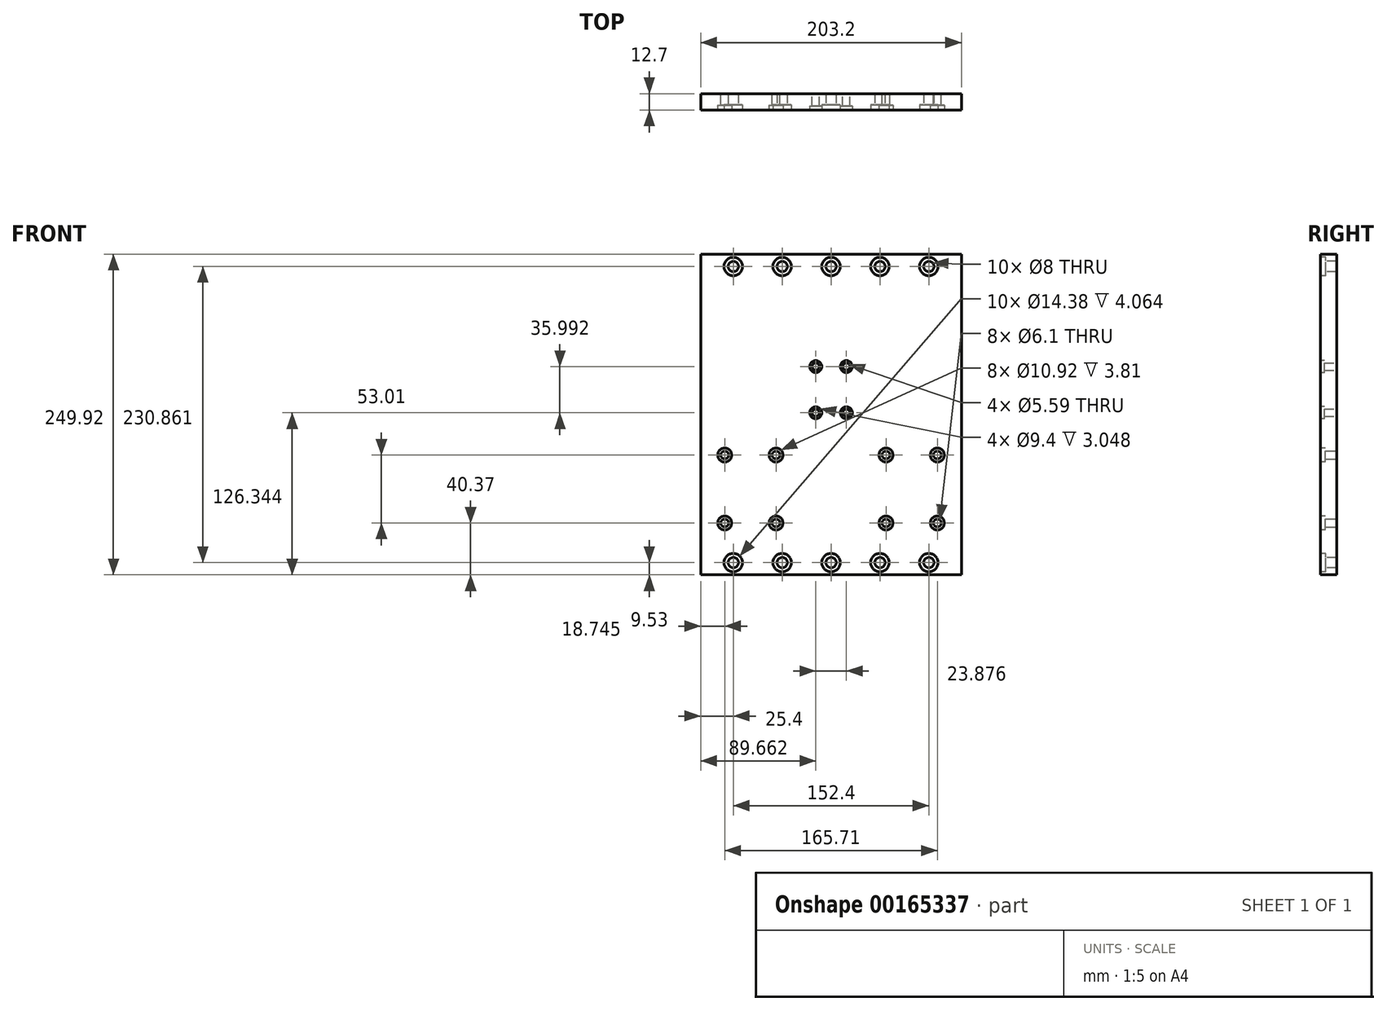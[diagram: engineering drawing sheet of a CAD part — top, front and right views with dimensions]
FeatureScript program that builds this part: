
annotation { "Feature Type Name" : "Feature", "Feature Type Description" : "" }
export const myFeature = defineFeature(function(context is Context, id is Id, definition is map)
    precondition{}
    {
        {
            var Q0;
            Q0=qCreatedBy(makeId("Front.planeOp"),FACE);
            var sketch = newSketch(context, id + "F0", { "sketchPlane" : qUnion([Q0])});
            skLineSegment(sketch, "E0.rect.bottom", {"start": v(101.6, 124.96) * mm, "end": v(-101.6, 124.96) * mm});
            skLineSegment(sketch, "E0.rect.top", {"start": v(101.6, -124.96) * mm, "end": v(-101.6, -124.96) * mm});
            skLineSegment(sketch, "E0.rect.left", {"start": v(101.6, 124.96) * mm, "end": v(101.6, -124.96) * mm});
            skLineSegment(sketch, "E0.rect.right", {"start": v(-101.6, 124.96) * mm, "end": v(-101.6, -124.96) * mm});
            skPoint(sketch, "E0.rect.middle", {"position": v(0, 0) * mm});
            skLineSegment(sketch, "E1", {"start": v(101.6, 112.26) * mm, "end": v(-101.6, 112.26) * mm, "construction": true});
            skLineSegment(sketch, "E2", {"start": v(101.6, -112.26) * mm, "end": v(-101.6, -112.26) * mm, "construction": true});
            skLineSegment(sketch, "E3", {"start": v(-11.94, 124.96) * mm, "end": v(-11.94, -124.96) * mm, "construction": true});
            skLineSegment(sketch, "E4.bottom", {"start": v(-11.94, 112.26) * mm, "end": v(11.94, 112.26) * mm, "construction": true});
            skLineSegment(sketch, "E4.left", {"start": v(-11.94, 112.26) * mm, "end": v(-11.94, 76.26) * mm, "construction": true});
            skLineSegment(sketch, "E4.right", {"start": v(11.94, 112.26) * mm, "end": v(11.94, 76.26) * mm, "construction": true});
            skLineSegment(sketch, "E5", {"start": v(11.94, 124.96) * mm, "end": v(11.94, -124.96) * mm, "construction": true});
            skLineSegment(sketch, "E6", {"start": v(-101.6, 1.38) * mm, "end": v(101.6, 1.38) * mm, "construction": true});
            skLineSegment(sketch, "E7", {"start": v(-101.6, 37.38) * mm, "end": v(101.6, 37.38) * mm, "construction": true});
            skCircle(sketch, "E8", {"center": v(-11.94, 37.38) * mm, "radius": 2.8 * mm});
            skCircle(sketch, "E9", {"center": v(11.94, 37.38) * mm, "radius": 2.8 * mm});
            skCircle(sketch, "E10", {"center": v(-11.94, 1.38) * mm, "radius": 2.8 * mm});
            skCircle(sketch, "E11", {"center": v(11.94, 1.38) * mm, "radius": 2.8 * mm});
            skSolve(sketch);
        }
        {
            var Q0;
            Q0=qSketchRegion(id+"F0",true);
            extrude(context, id + "F1", {"entities" : qUnion([Q0]), "depth" : 12.7 * mm});
        }
        {
            var Q0;
            Q0=makeQuery(id+"F1.opExtrude","CAP_FACE",FACE,{"disambiguationData":[OSD([sQuery(id+"F0.wireOp",EDGE,"E0.rect.bottom"),sQuery(id+"F0.wireOp",EDGE,"E0.rect.top"),sQuery(id+"F0.wireOp",EDGE,"E0.rect.left"),sQuery(id+"F0.wireOp",EDGE,"E0.rect.right"),sQuery(id+"F0.wireOp",EDGE,"8fd6003c-c3e5-4104-bfaa-be9952ec9e42"),sQuery(id+"F0.wireOp",EDGE,"85de903b-7077-4fb2-a5dd-9b00dc729731"),sQuery(id+"F0.wireOp",EDGE,"d51e1711-b5ba-43c6-b441-8d78bd74f6b7"),sQuery(id+"F0.wireOp",EDGE,"2b9548f0-683a-4c88-97d9-80483cf9402c")])],"isStart":false});
            var sketch = newSketch(context, id + "F2", { "sketchPlane" : qUnion([Q0])});
            skLineSegment(sketch, "E12", {"start": v(-101.6, 115.43) * mm, "end": v(101.6, 115.43) * mm, "construction": true});
            skLineSegment(sketch, "E13", {"start": v(-101.6, -115.43) * mm, "end": v(101.6, -115.43) * mm, "construction": true});
            skLineSegment(sketch, "E14", {"start": v(101.6, -115.43) * mm, "end": v(101.45, -116.98) * mm, "construction": true});
            skLineSegment(sketch, "E15", {"start": v(-76.2, 124.96) * mm, "end": v(-76.2, -124.96) * mm, "construction": true});
            skLineSegment(sketch, "E16", {"start": v(-38.1, 124.96) * mm, "end": v(-38.1, -124.96) * mm, "construction": true});
            skLineSegment(sketch, "E17", {"start": v(0, 124.96) * mm, "end": v(0, -124.96) * mm, "construction": true});
            skLineSegment(sketch, "E18", {"start": v(38.1, 124.96) * mm, "end": v(38.1, -124.96) * mm, "construction": true});
            skLineSegment(sketch, "E19", {"start": v(76.2, 124.96) * mm, "end": v(76.2, -124.96) * mm, "construction": true});
            skLineSegment(sketch, "E20", {"start": v(76.2, -124.96) * mm, "end": v(77.68, -126.6) * mm, "construction": true});
            skCircle(sketch, "E21", {"center": v(-76.2, 115.43) * mm, "radius": 4 * mm});
            skCircle(sketch, "E22", {"center": v(-38.1, 115.43) * mm, "radius": 4 * mm});
            skCircle(sketch, "E23", {"center": v(0, 115.43) * mm, "radius": 4 * mm});
            skCircle(sketch, "E24", {"center": v(38.1, 115.43) * mm, "radius": 4 * mm});
            skCircle(sketch, "E25", {"center": v(76.2, 115.43) * mm, "radius": 4 * mm});
            skCircle(sketch, "E26", {"center": v(-76.2, -115.43) * mm, "radius": 4 * mm});
            skCircle(sketch, "E27", {"center": v(-38.1, -115.43) * mm, "radius": 4 * mm});
            skCircle(sketch, "E28", {"center": v(0, -115.43) * mm, "radius": 4 * mm});
            skCircle(sketch, "E29", {"center": v(38.1, -115.43) * mm, "radius": 4 * mm});
            skCircle(sketch, "E30", {"center": v(76.2, -115.43) * mm, "radius": 4 * mm});
            skSolve(sketch);
        }
        {
            var Q0;
            Q0=qSketchRegion(id+"F2",true);
            extrude(context, id + "F3", {"entities" : qUnion([Q0]), "operationType" : NewBodyOperationType.REMOVE, "endBound" : BoundingType.THROUGH_ALL, "oppositeDirection" : true, "depth" : 25.4 * mm});
        }
        {
            var Q0;
            Q0=makeQuery(id+"F1.opExtrude","CAP_FACE",FACE,{"disambiguationData":[OSD([sQuery(id+"F0.wireOp",EDGE,"E0.rect.bottom"),sQuery(id+"F0.wireOp",EDGE,"E0.rect.top"),sQuery(id+"F0.wireOp",EDGE,"E0.rect.left"),sQuery(id+"F0.wireOp",EDGE,"E0.rect.right"),sQuery(id+"F0.wireOp",EDGE,"8fd6003c-c3e5-4104-bfaa-be9952ec9e42"),sQuery(id+"F0.wireOp",EDGE,"85de903b-7077-4fb2-a5dd-9b00dc729731"),sQuery(id+"F0.wireOp",EDGE,"d51e1711-b5ba-43c6-b441-8d78bd74f6b7"),sQuery(id+"F0.wireOp",EDGE,"2b9548f0-683a-4c88-97d9-80483cf9402c")])],"isStart":true});
            var sketch = newSketch(context, id + "F4", { "sketchPlane" : qUnion([Q0])});
            skLineSegment(sketch, "E31", {"start": v(101.6, -84.59) * mm, "end": v(-101.6, -84.59) * mm, "construction": true});
            skLineSegment(sketch, "E32", {"start": v(82.85, -124.96) * mm, "end": v(82.85, 124.96) * mm, "construction": true});
            skLineSegment(sketch, "E33", {"start": v(-82.85, 124.96) * mm, "end": v(-82.85, -124.96) * mm, "construction": true});
            skLineSegment(sketch, "E34", {"start": v(101.6, -31.58) * mm, "end": v(-101.6, -31.58) * mm, "construction": true});
            skLineSegment(sketch, "E35", {"start": v(42.85, -124.96) * mm, "end": v(42.85, 124.96) * mm, "construction": true});
            skLineSegment(sketch, "E36", {"start": v(-42.85, 124.96) * mm, "end": v(-42.85, -124.96) * mm, "construction": true});
            skCircle(sketch, "E37", {"center": v(82.85, -31.58) * mm, "radius": 3.05 * mm});
            skCircle(sketch, "E38", {"center": v(42.85, -31.58) * mm, "radius": 3.05 * mm});
            skCircle(sketch, "E39", {"center": v(82.85, -84.59) * mm, "radius": 3.05 * mm});
            skCircle(sketch, "E40", {"center": v(42.85, -84.59) * mm, "radius": 3.05 * mm});
            skCircle(sketch, "E41", {"center": v(-42.85, -31.58) * mm, "radius": 3.05 * mm});
            skCircle(sketch, "E42", {"center": v(-82.85, -31.58) * mm, "radius": 3.05 * mm});
            skCircle(sketch, "E43", {"center": v(-82.85, -84.59) * mm, "radius": 3.05 * mm});
            skCircle(sketch, "E44", {"center": v(-42.85, -84.59) * mm, "radius": 3.05 * mm});
            skSolve(sketch);
        }
        {
            var Q0;
            Q0=qSketchRegion(id+"F4",true);
            extrude(context, id + "F5", {"entities" : qUnion([Q0]), "operationType" : NewBodyOperationType.REMOVE, "endBound" : BoundingType.THROUGH_ALL, "oppositeDirection" : true, "depth" : 25.4 * mm});
        }
        {
            var Q0;
            Q0=qSketchRegion(id+"F0",true);
            extrude(context, id + "F6", {"entities" : qUnion([Q0]), "operationType" : NewBodyOperationType.REMOVE, "endBound" : BoundingType.THROUGH_ALL, "oppositeDirection" : true, "depth" : 25.4 * mm});
        }
        {
            var Q0;
            Q0=makeQuery(id+"F1.opExtrude","CAP_FACE",FACE,{"disambiguationData":[OSD([sQuery(id+"F0.wireOp",EDGE,"E0.rect.bottom"),sQuery(id+"F0.wireOp",EDGE,"E0.rect.top"),sQuery(id+"F0.wireOp",EDGE,"E0.rect.left"),sQuery(id+"F0.wireOp",EDGE,"E0.rect.right"),sQuery(id+"F0.wireOp",EDGE,"E8"),sQuery(id+"F0.wireOp",EDGE,"E9"),sQuery(id+"F0.wireOp",EDGE,"E10"),sQuery(id+"F0.wireOp",EDGE,"E11")])],"isStart":false});
            var sketch = newSketch(context, id + "F7", { "sketchPlane" : qUnion([Q0])});
            skCircle(sketch, "E45", {"center": v(-76.2, -115.43) * mm, "radius": 7.19 * mm});
            skCircle(sketch, "E46", {"center": v(-38.1, -115.43) * mm, "radius": 7.19 * mm});
            skCircle(sketch, "E47", {"center": v(0, -115.43) * mm, "radius": 7.19 * mm});
            skCircle(sketch, "E48", {"center": v(38.1, -115.43) * mm, "radius": 7.19 * mm});
            skCircle(sketch, "E49", {"center": v(76.2, -115.43) * mm, "radius": 7.19 * mm});
            skCircle(sketch, "E50", {"center": v(-76.2, 115.43) * mm, "radius": 7.19 * mm});
            skCircle(sketch, "E51", {"center": v(-38.1, 115.43) * mm, "radius": 7.19 * mm});
            skCircle(sketch, "E52", {"center": v(0, 115.43) * mm, "radius": 7.19 * mm});
            skCircle(sketch, "E53", {"center": v(38.1, 115.43) * mm, "radius": 7.19 * mm});
            skCircle(sketch, "E54", {"center": v(76.2, 115.43) * mm, "radius": 7.19 * mm});
            skSolve(sketch);
        }
        {
            var Q0;
            Q0=qSketchRegion(id+"F7",true);
            extrude(context, id + "F8", {"entities" : qUnion([Q0]), "operationType" : NewBodyOperationType.REMOVE, "oppositeDirection" : true, "depth" : 4.06 * mm});
        }
        {
            var Q0;
            Q0=makeQuery(id+"F1.opExtrude","CAP_FACE",FACE,{"disambiguationData":[OSD([sQuery(id+"F0.wireOp",EDGE,"E0.rect.bottom"),sQuery(id+"F0.wireOp",EDGE,"E0.rect.top"),sQuery(id+"F0.wireOp",EDGE,"E0.rect.left"),sQuery(id+"F0.wireOp",EDGE,"E0.rect.right"),sQuery(id+"F0.wireOp",EDGE,"E8"),sQuery(id+"F0.wireOp",EDGE,"E9"),sQuery(id+"F0.wireOp",EDGE,"E10"),sQuery(id+"F0.wireOp",EDGE,"E11")])],"isStart":false});
            var sketch = newSketch(context, id + "F9", { "sketchPlane" : qUnion([Q0])});
            skCircle(sketch, "E55", {"center": v(-11.94, 37.38) * mm, "radius": 4.7 * mm});
            skCircle(sketch, "E56", {"center": v(11.94, 37.38) * mm, "radius": 4.7 * mm});
            skCircle(sketch, "E57", {"center": v(11.94, 1.38) * mm, "radius": 4.7 * mm});
            skCircle(sketch, "E58", {"center": v(-11.94, 1.38) * mm, "radius": 4.7 * mm});
            skSolve(sketch);
        }
        {
            var Q0;
            Q0=qSketchRegion(id+"F9",true);
            extrude(context, id + "F10", {"entities" : qUnion([Q0]), "operationType" : NewBodyOperationType.REMOVE, "oppositeDirection" : true, "depth" : 3.05 * mm});
        }
        {
            var Q0;
            Q0=makeQuery(id+"F1.opExtrude","CAP_FACE",FACE,{"disambiguationData":[OSD([sQuery(id+"F0.wireOp",EDGE,"E0.rect.bottom"),sQuery(id+"F0.wireOp",EDGE,"E0.rect.top"),sQuery(id+"F0.wireOp",EDGE,"E0.rect.left"),sQuery(id+"F0.wireOp",EDGE,"E0.rect.right"),sQuery(id+"F0.wireOp",EDGE,"E8"),sQuery(id+"F0.wireOp",EDGE,"E9"),sQuery(id+"F0.wireOp",EDGE,"E10"),sQuery(id+"F0.wireOp",EDGE,"E11")])],"isStart":false});
            var sketch = newSketch(context, id + "F11", { "sketchPlane" : qUnion([Q0])});
            skCircle(sketch, "E59", {"center": v(-82.85, -31.58) * mm, "radius": 5.46 * mm});
            skCircle(sketch, "E60", {"center": v(-42.85, -31.58) * mm, "radius": 5.46 * mm});
            skCircle(sketch, "E61", {"center": v(42.85, -31.58) * mm, "radius": 5.46 * mm});
            skCircle(sketch, "E62", {"center": v(82.85, -31.58) * mm, "radius": 5.46 * mm});
            skCircle(sketch, "E63", {"center": v(82.85, -84.59) * mm, "radius": 5.46 * mm});
            skCircle(sketch, "E64", {"center": v(42.85, -84.59) * mm, "radius": 5.46 * mm});
            skCircle(sketch, "E65", {"center": v(-42.85, -84.59) * mm, "radius": 5.46 * mm});
            skCircle(sketch, "E66", {"center": v(-82.85, -84.59) * mm, "radius": 5.46 * mm});
            skSolve(sketch);
        }
        {
            var Q0;
            Q0=qSketchRegion(id+"F11",true);
            extrude(context, id + "F12", {"entities" : qUnion([Q0]), "operationType" : NewBodyOperationType.REMOVE, "oppositeDirection" : true, "depth" : 3.8 * mm});
        }
    });
